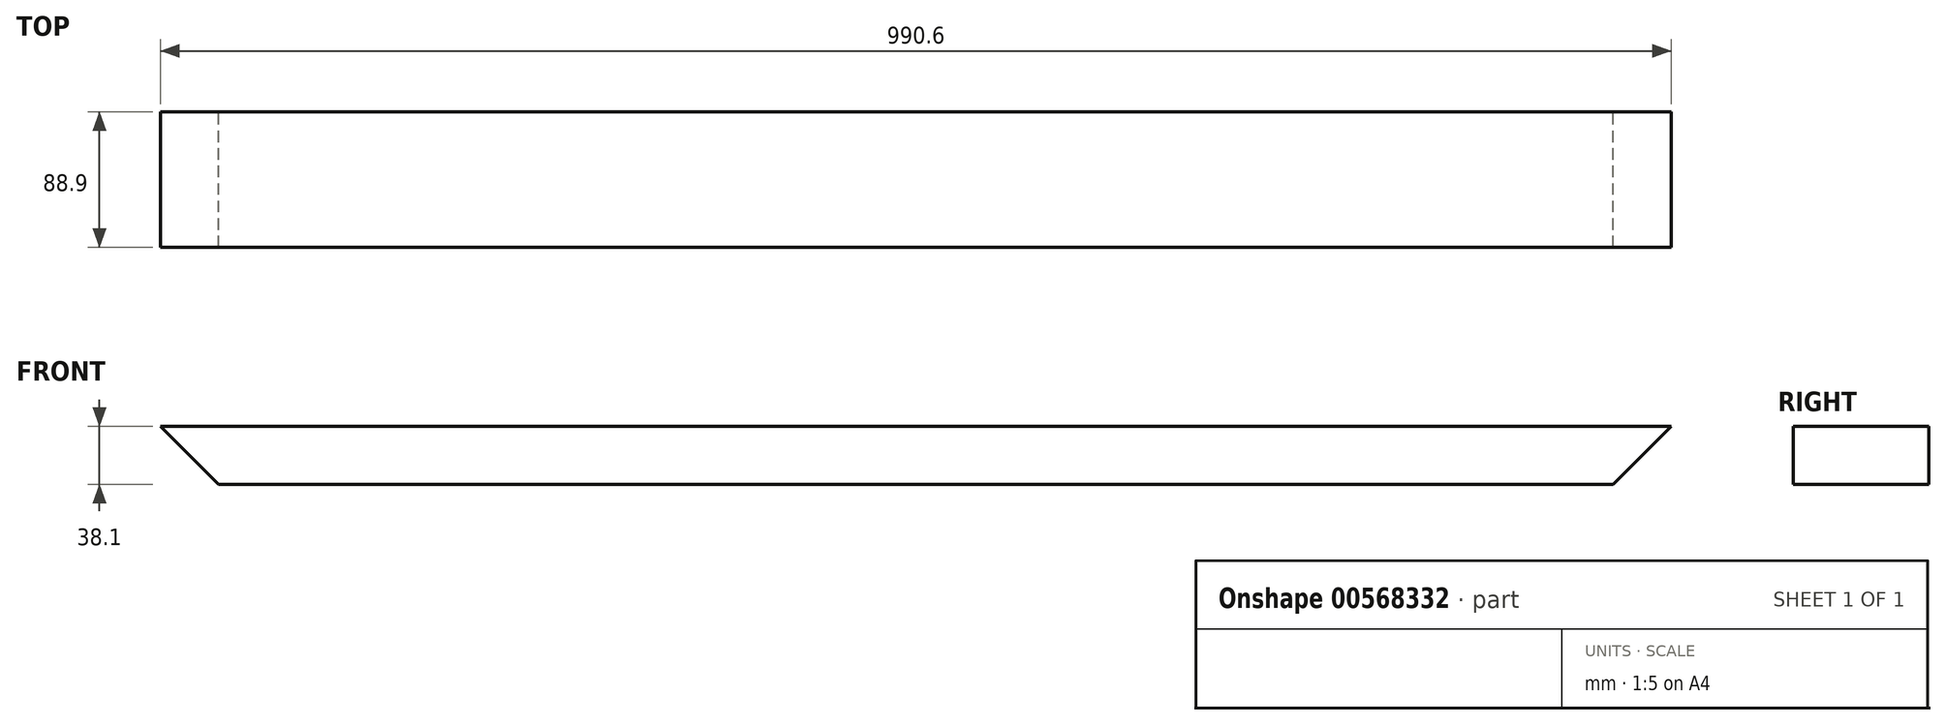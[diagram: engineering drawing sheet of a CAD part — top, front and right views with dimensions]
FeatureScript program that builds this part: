
annotation { "Feature Type Name" : "Feature", "Feature Type Description" : "" }
export const myFeature = defineFeature(function(context is Context, id is Id, definition is map)
    precondition{}
    {
        {
            var Q0;
            Q0=qCreatedBy(makeId("Front.planeOp"),FACE);
            var sketch = newSketch(context, id + "F0", { "sketchPlane" : qUnion([Q0])});
            skLineSegment(sketch, "E0", {"start": v(0, 0) * mm, "end": v(513.13, 0) * mm});
            skLineSegment(sketch, "E1", {"start": v(513.13, 0) * mm, "end": v(551.23, 38.1) * mm});
            skLineSegment(sketch, "E2", {"start": v(551.23, 38.1) * mm, "end": v(-439.37, 38.1) * mm});
            skLineSegment(sketch, "E3", {"start": v(-439.37, 38.1) * mm, "end": v(-401.27, 0) * mm});
            skLineSegment(sketch, "E4", {"start": v(-401.27, 0) * mm, "end": v(0, 0) * mm});
            skSolve(sketch);
        }
        {
            var Q0;
            Q0 = qSketchRegion(id + "F0", true);
            extrude(context, id + "F1", {"entities" : qUnion([Q0]), "depth" : 88.9 * mm, "offsetDistance" : 25.4 * mm});
        }
    });
